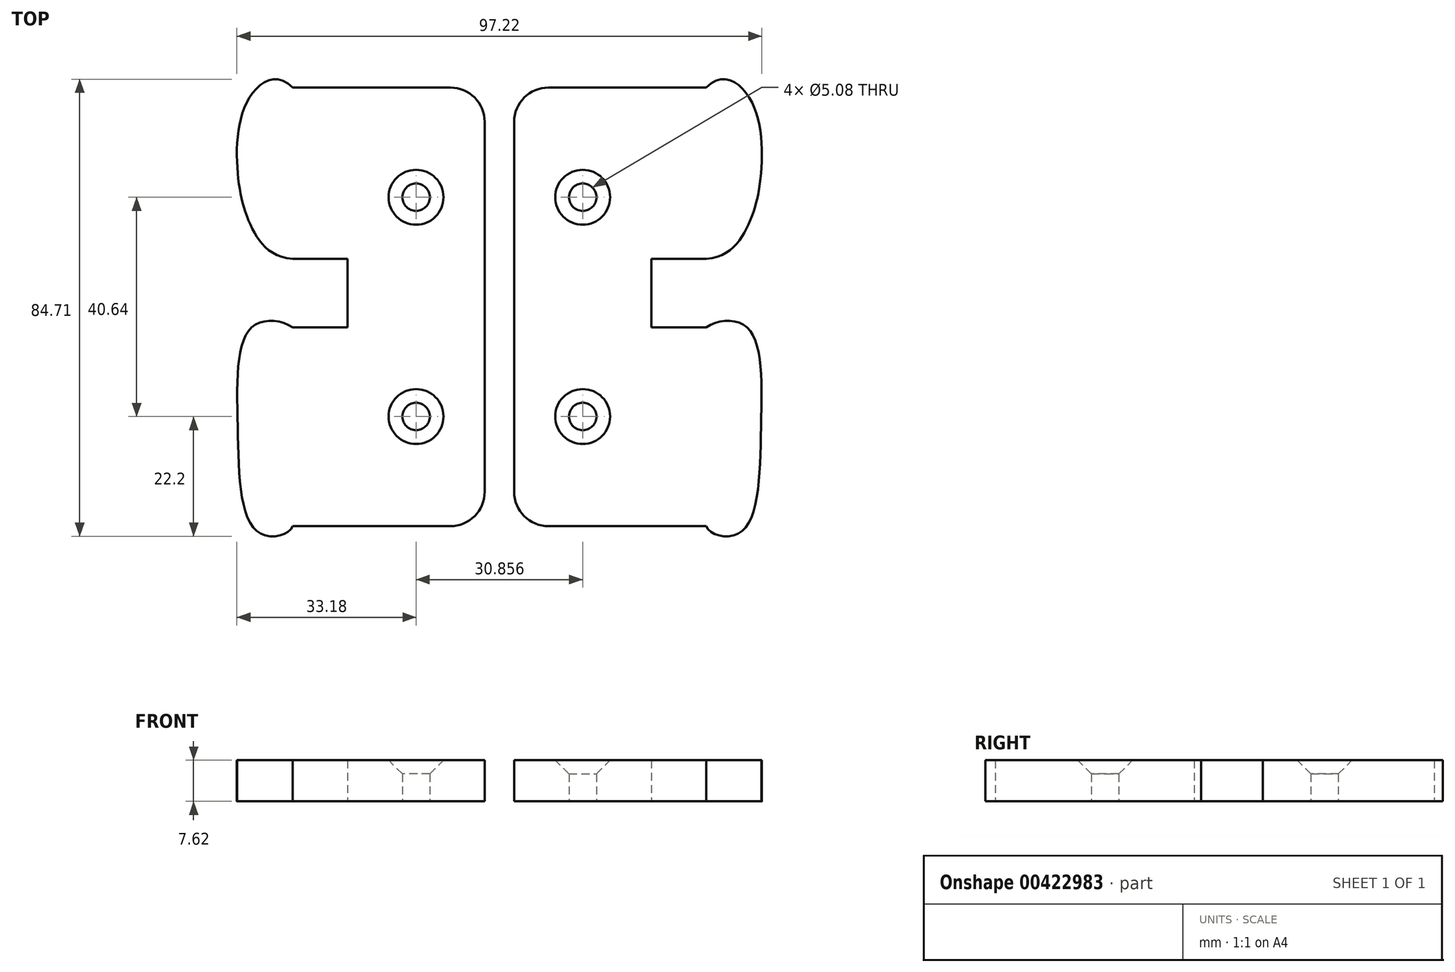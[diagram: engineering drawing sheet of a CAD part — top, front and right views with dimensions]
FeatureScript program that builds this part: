
annotation { "Feature Type Name" : "Feature", "Feature Type Description" : "" }
export const myFeature = defineFeature(function(context is Context, id is Id, definition is map)
    precondition{}
    {
        {
            var Q0;
            Q0=qCreatedBy(makeId("Top.planeOp"),FACE);
            var sketch = newSketch(context, id + "F0", { "sketchPlane" : qUnion([Q0])});
            skLineSegment(sketch, "E0.bottom", {"start": v(0, 0) * mm, "end": v(25.4, 0) * mm});
            skLineSegment(sketch, "E0.top", {"start": v(0, 81.28) * mm, "end": v(25.4, 81.28) * mm});
            skLineSegment(sketch, "E0.left", {"start": v(0, 0) * mm, "end": v(0, 81.28) * mm});
            skLineSegment(sketch, "E0.right", {"start": v(25.4, 0) * mm, "end": v(25.4, 81.28) * mm});
            skLineSegment(sketch, "E1", {"start": v(0, 81.28) * mm, "end": v(-10.16, 81.28) * mm});
            skLineSegment(sketch, "E2", {"start": v(0, 81.28) * mm, "end": v(0, 36.83) * mm});
            skLineSegment(sketch, "E3", {"start": v(0, 36.83) * mm, "end": v(-10.16, 36.83) * mm});
            skLineSegment(sketch, "E4", {"start": v(0, 0) * mm, "end": v(-10.16, 0) * mm});
            skLineSegment(sketch, "E5", {"start": v(0, 36.83) * mm, "end": v(0, 49.53) * mm});
            skLineSegment(sketch, "E6", {"start": v(0, 49.53) * mm, "end": v(-10.16, 49.53) * mm});
            skFitSpline(sketch, "E7", {"points": [v(-10.16, 0) * mm, v(-16.24, -1.3) * mm, v(-20.32, 18.41) * mm, v(-17.7, 36.85) * mm, v(-10.16, 36.83) * mm], "startDerivative": vector(-10.25, -28.1) * mm, "endDerivative": vector(35.24, -23.16) * mm});
            skLineSegment(sketch, "E8", {"start": v(0, 81.28) * mm, "end": v(0, 49.53) * mm});
            skLineSegment(sketch, "E9", {"start": v(0, 36.83) * mm, "end": v(0, 0) * mm});
            skLineSegment(sketch, "E10", {"start": v(0, 18.42) * mm, "end": v(-20.32, 18.42) * mm});
            skLineSegment(sketch, "E11", {"start": v(0, 65.4) * mm, "end": v(-20.32, 65.4) * mm});
            skFitSpline(sketch, "E12", {"points": [v(-10.16, 49.53) * mm, v(-17.7, 55.28) * mm, v(-20.32, 65.4) * mm, v(-18.07, 79.56) * mm, v(-10.16, 81.28) * mm], "startDerivative": vector(-52.6, 4.32) * mm, "endDerivative": vector(40.67, -41.27) * mm});
            skLineSegment(sketch, "E13", {"start": v(12.7, 81.28) * mm, "end": v(12.7, 60.96) * mm});
            skLineSegment(sketch, "E14", {"start": v(12.7, 0) * mm, "end": v(12.7, 20.32) * mm});
            skCircle(sketch, "E15", {"center": v(12.7, 60.96) * mm, "radius": 2.54 * mm});
            skCircle(sketch, "E16", {"center": v(12.7, 20.32) * mm, "radius": 2.54 * mm});
            skSolve(sketch);
        }
        {
            var Q0;
            {var subQ5=sQuery(id+"F0.wireOp",EDGE,"E0.right");Q0=makeQuery(id+"F0.imprint","IMPRINT",FACE,{"disambiguationData":[TD([[makeQuery(id+"F0.imprint","IMPRINT",EDGE,{"derivedFrom":subQ5}),1.0]])]});}
            var Q1;
            {var subQ0=sQuery(id+"F0.wireOp",EDGE,"E6");Q1=makeQuery(id+"F0.imprint","IMPRINT",FACE,{"disambiguationData":[TD([[makeQuery(id+"F0.imprint","IMPRINT",EDGE,{"derivedFrom":subQ0}),-1.0]])]});}
            var Q2;
            {var subQ0=sQuery(id+"F0.wireOp",EDGE,"E1");Q2=makeQuery(id+"F0.imprint","IMPRINT",FACE,{"disambiguationData":[TD([[makeQuery(id+"F0.imprint","IMPRINT",EDGE,{"derivedFrom":subQ0}),1.0]])]});}
            var Q3;
            {var subQ0=sQuery(id+"F0.wireOp",EDGE,"E3");Q3=makeQuery(id+"F0.imprint","IMPRINT",FACE,{"disambiguationData":[TD([[makeQuery(id+"F0.imprint","IMPRINT",EDGE,{"derivedFrom":subQ0}),1.0]])]});}
            var Q4;
            {var subQ0=sQuery(id+"F0.wireOp",EDGE,"E4");Q4=makeQuery(id+"F0.imprint","IMPRINT",FACE,{"disambiguationData":[TD([[makeQuery(id+"F0.imprint","IMPRINT",EDGE,{"derivedFrom":subQ0}),-1.0]])]});}
            extrude(context, id + "F1", {"entities" : qUnion([Q0, Q1, Q2, Q3, Q4]), "depth" : 7.62 * mm});
        }
        {
            var Q0;
            Q0=makeQuery(id+"F1.opExtrude","SWEPT_EDGE",EDGE,{"disambiguationData":[OSD([sQuery(id+"F0.wireOp",EDGE,"E0.bottom"),sQuery(id+"F0.wireOp",EDGE,"E0.right")])]});
            var Q1;
            Q1=makeQuery(id+"F1.opExtrude","SWEPT_EDGE",EDGE,{"disambiguationData":[OSD([sQuery(id+"F0.wireOp",EDGE,"E0.top"),sQuery(id+"F0.wireOp",EDGE,"E0.right")])]});
            fillet(context, id + "F2", {"entities" : qUnion([Q0, Q1]), "radius" : 6.35 * mm, "tangentPropagation" : true, "allowEdgeOverflow" : false});
        }
        {
            var Q0;
            Q0=makeQuery(id+"F1.opExtrude","CAP_EDGE",EDGE,{"disambiguationData":[OSD([sQuery(id+"F0.wireOp",EDGE,"E15")])],"isStart":false});
            var Q1;
            Q1=makeQuery(id+"F1.opExtrude","CAP_EDGE",EDGE,{"disambiguationData":[OSD([sQuery(id+"F0.wireOp",EDGE,"E16")])],"isStart":false});
            chamfer(context, id + "F3", {"entities" : qUnion([Q0, Q1]), "width" : 2.54 * mm, "tangentPropagation" : true});
        }
        {
            var Q0;
            Q0=qCreatedBy(makeId("Top.planeOp"),FACE);
            var sketch = newSketch(context, id + "F4", { "sketchPlane" : qUnion([Q0])});
            skLineSegment(sketch, "E17", {"start": v(28.13, 0) * mm, "end": v(28.13, 83.65) * mm});
            skSolve(sketch);
        }
        {
            var Q0;
            Q0=sQuery(id+"F4.wireOp",EDGE,"E17");
            extrude(context, id + "F5", {"bodyType" : ToolBodyType.SURFACE, "surfaceEntities" : qUnion([Q0]), "depth" : 25.4 * mm});
        }
        {
            var Q0;
            Q0=makeQuery(id+"F1.opExtrude","SWEPT_BODY",BODY,{"disambiguationData":[OSD([sQuery(id+"F0.wireOp",EDGE,"E0.bottom"),sQuery(id+"F0.wireOp",EDGE,"E0.top"),sQuery(id+"F0.wireOp",EDGE,"E0.right"),sQuery(id+"F0.wireOp",EDGE,"E1"),sQuery(id+"F0.wireOp",EDGE,"E3"),sQuery(id+"F0.wireOp",EDGE,"E4"),sQuery(id+"F0.wireOp",EDGE,"E5"),sQuery(id+"F0.wireOp",EDGE,"E6"),sQuery(id+"F0.wireOp",EDGE,"E7"),sQuery(id+"F0.wireOp",EDGE,"E12"),sQuery(id+"F0.wireOp",EDGE,"E15"),sQuery(id+"F0.wireOp",EDGE,"E16")])]});
            var Q1;
            Q1=makeQuery(id+"F5.opExtrude","SWEPT_FACE",FACE,{"disambiguationData":[OSD([sQuery(id+"F4.wireOp",EDGE,"E17")])]});
            mirror(context, id + "F6", {"entities" : qUnion([Q0]), "mirrorPlane" : qUnion([Q1])});
        }
    });
